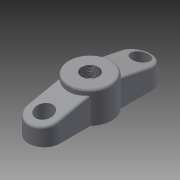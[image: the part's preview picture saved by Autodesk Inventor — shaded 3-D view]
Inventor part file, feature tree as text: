
AUTODESK INVENTOR PART (.ipt)
format: ipt  version: 2015 (Build 190159000, 159)  size: 177,664 bytes
history: native  units: in
note: dims shown in document units (in); Inventor stores cm internally (conversion verified against a paired STEP export)
features: extrude x4, sketch x4, fillet x3, thread x1
ambient origin geometry x8: Origin, YZ Plane, XZ Plane, XY Plane, X Axis, Y Axis, Z Axis, Center Point
bodies: Body1 (feature_tree)
feature tree (12):
  extrude  "Extrusion4"  Depth=2.7559in
  fillet  "Fillet1"  Radius=20.0787in
  extrude  "Extrusion5"  Depth=2.3622in
  extrude  "Extrusion6"  Depth=5.1181in TaperAngle=0.0deg
  extrude  "Extrusion7"  Depth=0.3937in
  thread  "Thread1"  [1 undecoded]
  fillet  "Fillet2"  Radius=14.9606in
  fillet  "Fillet3"  Radius=2.7559in
  sketch  "Sketch5"  dims[d9=20.0787in d10=2.7559in d11=20.0787in]
  sketch  "Sketch6"  dims[d12=4.3307in d13=2.3622in]
  sketch  "Sketch7"  dims[d14=2.3622in d17=5.1181in d18=0.0in]
  sketch  "Sketch8"  dims[d19=2.5591in d20=2.5591in d21=2.5591in d22=14.9606in d23=2.7559in d24=2.7559in d25=2.7559in d26=5.1181in d27=0.0in d28=2.5591in d29=7.0866in d30=5.1181in d31=0.0in d32=2.7559in d33=5.1181in d34=0.0in d35=0.3937in d36=0.0in d37=0.3937in d38=0.3937in]
note: 1 required parameter value undecoded (feature->parameter linkage not recoverable at this tier; creation-order binding heuristic only, values carry confidence <= 0.55)
